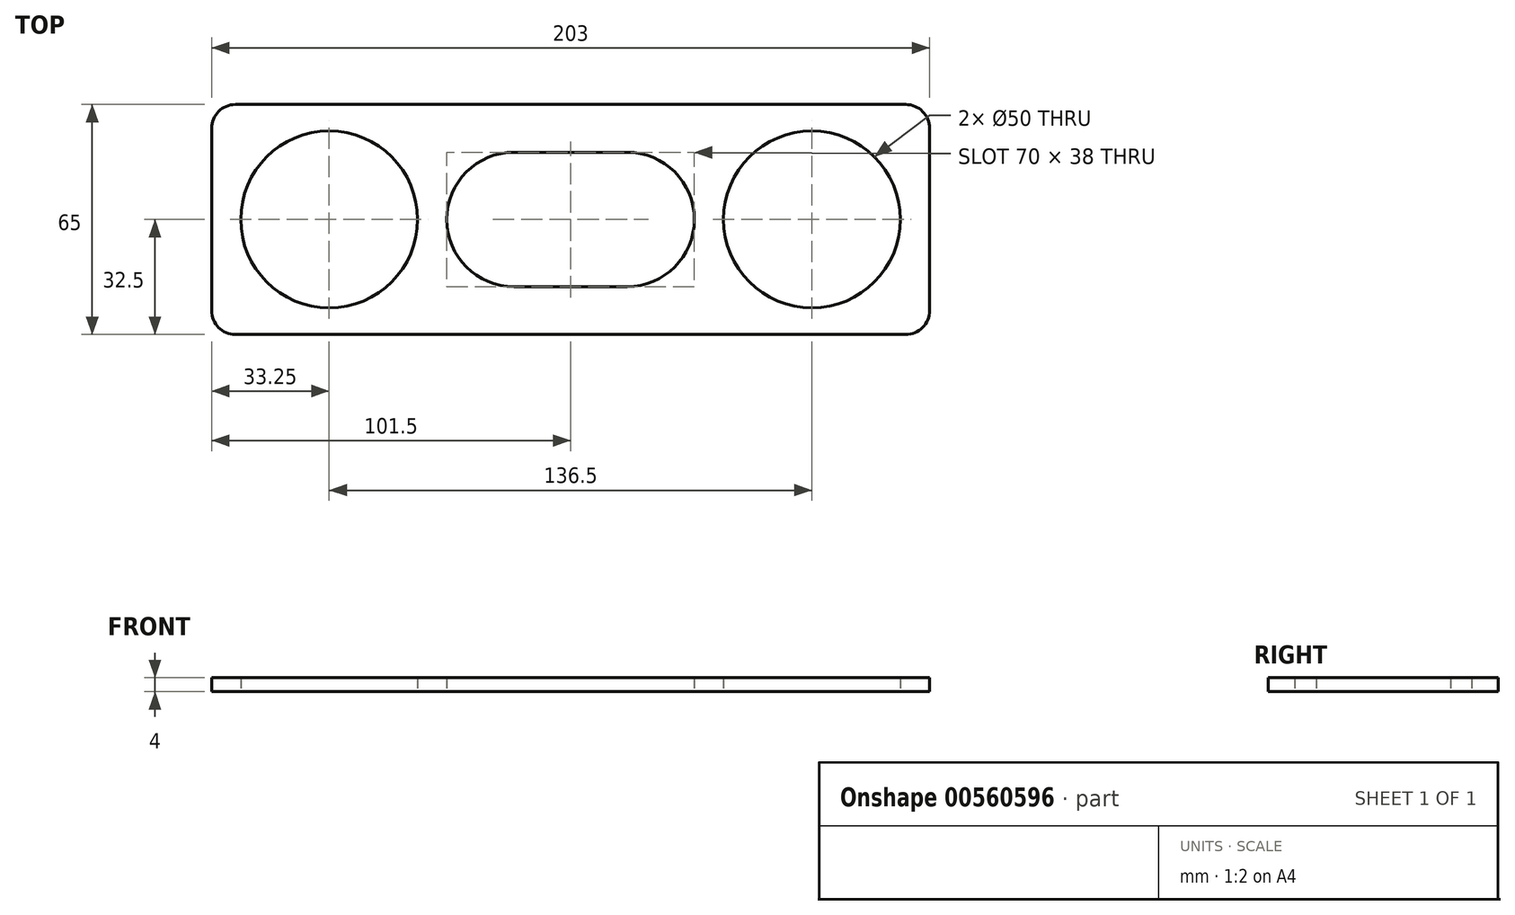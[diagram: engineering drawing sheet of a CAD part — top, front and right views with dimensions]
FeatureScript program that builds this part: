
annotation { "Feature Type Name" : "Feature", "Feature Type Description" : "" }
export const myFeature = defineFeature(function(context is Context, id is Id, definition is map)
    precondition{}
    {
        {
            var Q0;
            Q0=qCreatedBy(makeId("Top.planeOp"),FACE);
            var sketch = newSketch(context, id + "F0", { "sketchPlane" : qUnion([Q0])});
            skLineSegment(sketch, "E0.bottom", {"start": v(94.75, -32.5) * mm, "end": v(-94.75, -32.5) * mm});
            skLineSegment(sketch, "E0.top", {"start": v(94.75, 32.5) * mm, "end": v(-94.75, 32.5) * mm});
            skLineSegment(sketch, "E0.left", {"start": v(101.5, -25.75) * mm, "end": v(101.5, 25.75) * mm});
            skLineSegment(sketch, "E0.right", {"start": v(-101.5, -25.75) * mm, "end": v(-101.5, 25.75) * mm});
            skPoint(sketch, "E1.orphan", {"position": v(-101.5, 32.5) * mm});
            skArc(sketch, "E2.trimOffspring", {"start": v(-94.75, 32.5) * mm, "mid": v(-99.52, 30.52) * mm, "end": v(-101.5, 25.75) * mm});
            skArc(sketch, "E3.MirrorCS", {"start": v(94.75, 32.5) * mm, "mid": v(99.52, 30.52) * mm, "end": v(101.5, 25.75) * mm});
            skArc(sketch, "E4.MirrorCS", {"start": v(-94.75, -32.5) * mm, "mid": v(-99.52, -30.52) * mm, "end": v(-101.5, -25.75) * mm});
            skArc(sketch, "E5.MirrorCS", {"start": v(94.75, -32.5) * mm, "mid": v(99.52, -30.52) * mm, "end": v(101.5, -25.75) * mm});
            skPoint(sketch, "E6.orphan", {"position": v(-101.5, -32.5) * mm});
            skPoint(sketch, "E7.orphan", {"position": v(101.5, -32.5) * mm});
            skPoint(sketch, "E8.orphan", {"position": v(101.5, 32.5) * mm});
            skLineSegment(sketch, "E9.bottom", {"start": v(16, -19) * mm, "end": v(-16, -19) * mm});
            skLineSegment(sketch, "E9.top", {"start": v(16, 19) * mm, "end": v(-16, 19) * mm});
            skLineSegment(sketch, "E9.left", {"start": v(16, -19) * mm, "end": v(16, 19) * mm});
            skLineSegment(sketch, "E9.right", {"start": v(-16, -19) * mm, "end": v(-16, 19) * mm});
            skPoint(sketch, "E9.middle", {"position": v(0, 0) * mm});
            skArc(sketch, "E10", {"start": v(-16, 19) * mm, "mid": v(-35, 0) * mm, "end": v(-16, -19) * mm});
            skArc(sketch, "E11", {"start": v(16, 19) * mm, "mid": v(35, 0) * mm, "end": v(16, -19) * mm});
            skCircle(sketch, "E12", {"center": v(-68.25, 0) * mm, "radius": 25 * mm});
            skLineSegment(sketch, "E13", {"start": v(0, 0) * mm, "end": v(0, 12.3) * mm, "construction": true});
            skCircle(sketch, "E14.MirrorC", {"center": v(68.25, 0) * mm, "radius": 25 * mm});
            skSolve(sketch);
        }
        {
            var Q0;
            Q0 = qSketchRegion(id + "F0", true);
            extrude(context, id + "F1", {"entities" : qUnion([Q0]), "depth" : 4 * mm, "offsetDistance" : 25 * mm});
        }
    });
